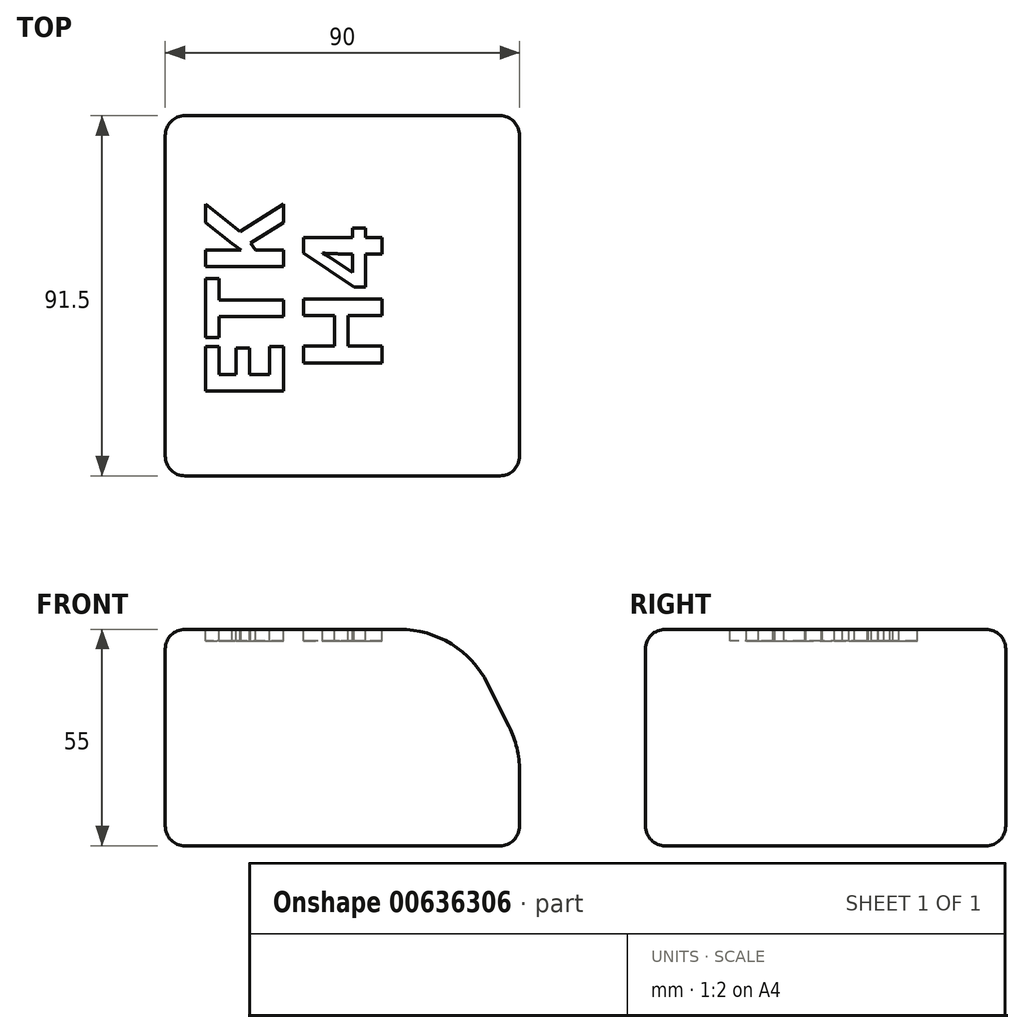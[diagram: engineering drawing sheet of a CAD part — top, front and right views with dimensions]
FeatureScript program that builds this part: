
annotation { "Feature Type Name" : "Feature", "Feature Type Description" : "" }
export const myFeature = defineFeature(function(context is Context, id is Id, definition is map)
    precondition{}
    {
        {
            var Q0;
            Q0=qCreatedBy(makeId("Front.planeOp"),FACE);
            var sketch = newSketch(context, id + "F0", { "sketchPlane" : qUnion([Q0])});
            skLineSegment(sketch, "E0", {"start": v(0, 0) * mm, "end": v(90, 0) * mm});
            skLineSegment(sketch, "E1", {"start": v(90, 0) * mm, "end": v(90, 19.1) * mm});
            skLineSegment(sketch, "E2", {"start": v(87.36, 30.28) * mm, "end": v(81.9, 41.18) * mm});
            skLineSegment(sketch, "E3", {"start": v(59.55, 55) * mm, "end": v(0, 55) * mm});
            skLineSegment(sketch, "E4", {"start": v(0, 55) * mm, "end": v(0, 0) * mm});
            skPoint(sketch, "E5.visualSharp", {"position": v(75, 55) * mm});
            skArc(sketch, "E5.filletArc", {"start": v(81.9, 41.18) * mm, "mid": v(72.7, 51.27) * mm, "end": v(59.55, 55) * mm});
            skPoint(sketch, "E6.visualSharp", {"position": v(90, 25) * mm});
            skArc(sketch, "E6.filletArc", {"start": v(90, 19.1) * mm, "mid": v(89.33, 24.84) * mm, "end": v(87.36, 30.28) * mm});
            skSolve(sketch);
        }
        {
            var Q0;
            Q0 = qSketchRegion(id + "F0", true);
            extrude(context, id + "F1", {"entities" : qUnion([Q0]), "depth" : 91.5 * mm, "offsetDistance" : 25 * mm});
        }
        {
            var Q0;
            Q0=makeQuery(id+"F1.opExtrude","CAP_EDGE",EDGE,{"disambiguationData":[OSD([sQuery(id+"F0.wireOp",EDGE,"E3")])],"isStart":false});
            var Q1;
            Q1=makeQuery(id+"F1.opExtrude","CAP_EDGE",EDGE,{"disambiguationData":[OSD([sQuery(id+"F0.wireOp",EDGE,"E4")])],"isStart":false});
            var Q2;
            Q2=makeQuery(id+"F1.opExtrude","CAP_EDGE",EDGE,{"disambiguationData":[OSD([sQuery(id+"F0.wireOp",EDGE,"E0")])],"isStart":false});
            var Q3;
            Q3=makeQuery(id+"F1.opExtrude","CAP_EDGE",EDGE,{"disambiguationData":[OSD([sQuery(id+"F0.wireOp",EDGE,"E3")])],"isStart":true});
            var Q4;
            Q4=makeQuery(id+"F1.opExtrude","CAP_EDGE",EDGE,{"disambiguationData":[OSD([sQuery(id+"F0.wireOp",EDGE,"E0")])],"isStart":true});
            var Q5;
            Q5=makeQuery(id+"F1.opExtrude","CAP_EDGE",EDGE,{"disambiguationData":[OSD([sQuery(id+"F0.wireOp",EDGE,"E4")])],"isStart":true});
            var Q6;
            Q6=makeQuery(id+"F1.opExtrude","SWEPT_EDGE",EDGE,{"disambiguationData":[OSD([sQuery(id+"F0.wireOp",EDGE,"E0"),sQuery(id+"F0.wireOp",EDGE,"E4")])]});
            var Q7;
            Q7=makeQuery(id+"F1.opExtrude","SWEPT_EDGE",EDGE,{"disambiguationData":[OSD([sQuery(id+"F0.wireOp",EDGE,"E3"),sQuery(id+"F0.wireOp",EDGE,"E4")])]});
            var Q8;
            Q8=makeQuery(id+"F1.opExtrude","SWEPT_EDGE",EDGE,{"disambiguationData":[OSD([sQuery(id+"F0.wireOp",EDGE,"E0"),sQuery(id+"F0.wireOp",EDGE,"E1")])]});
            fillet(context, id + "F2", {"entities" : qUnion([Q0, Q1, Q2, Q3, Q4, Q5, Q6, Q7, Q8]), "radius" : 5 * mm, "tangentPropagation" : true, "allowEdgeOverflow" : false});
        }
        {
            var Q0;
            Q0=makeQuery(id+"F1.opExtrude","SWEPT_FACE",FACE,{"disambiguationData":[OSD([sQuery(id+"F0.wireOp",EDGE,"E3")])]});
            var sketch = newSketch(context, id + "F3", { "sketchPlane" : qUnion([Q0])});
            skText(sketch, "E7", { "text": "ETK", "fontName": "OpenSans-Bold.ttf"});
            const initialGuessF3  = {"E7": [0.03, -0.0725, 0, 1, 0.02]};
            skSetInitialGuess(sketch, initialGuessF3);
            skSolve(sketch);
        }
        {
            var Q0;
            Q0=makeQuery(id+"F1.opExtrude","SWEPT_FACE",FACE,{"disambiguationData":[OSD([sQuery(id+"F0.wireOp",EDGE,"E3")])]});
            var sketch = newSketch(context, id + "F4", { "sketchPlane" : qUnion([Q0])});
            skText(sketch, "E8", { "text": " H4", "fontName": "OpenSans-Bold.ttf"});
            const initialGuessF4  = {"E8": [0.055, -0.0725, 0, 1, 0.02]};
            skSetInitialGuess(sketch, initialGuessF4);
            skSolve(sketch);
        }
        {
            var Q0;
            Q0 = qSketchRegion(id + "F3", true);
            var Q1;
            Q1 = qSketchRegion(id + "F4", true);
            extrude(context, id + "F5", {"entities" : qUnion([Q0, Q1]), "operationType" : NewBodyOperationType.REMOVE, "surfaceOperationType" : NewSurfaceOperationType.ADD, "oppositeDirection" : true, "depth" : 3 * mm, "offsetDistance" : 25 * mm});
        }
    });
